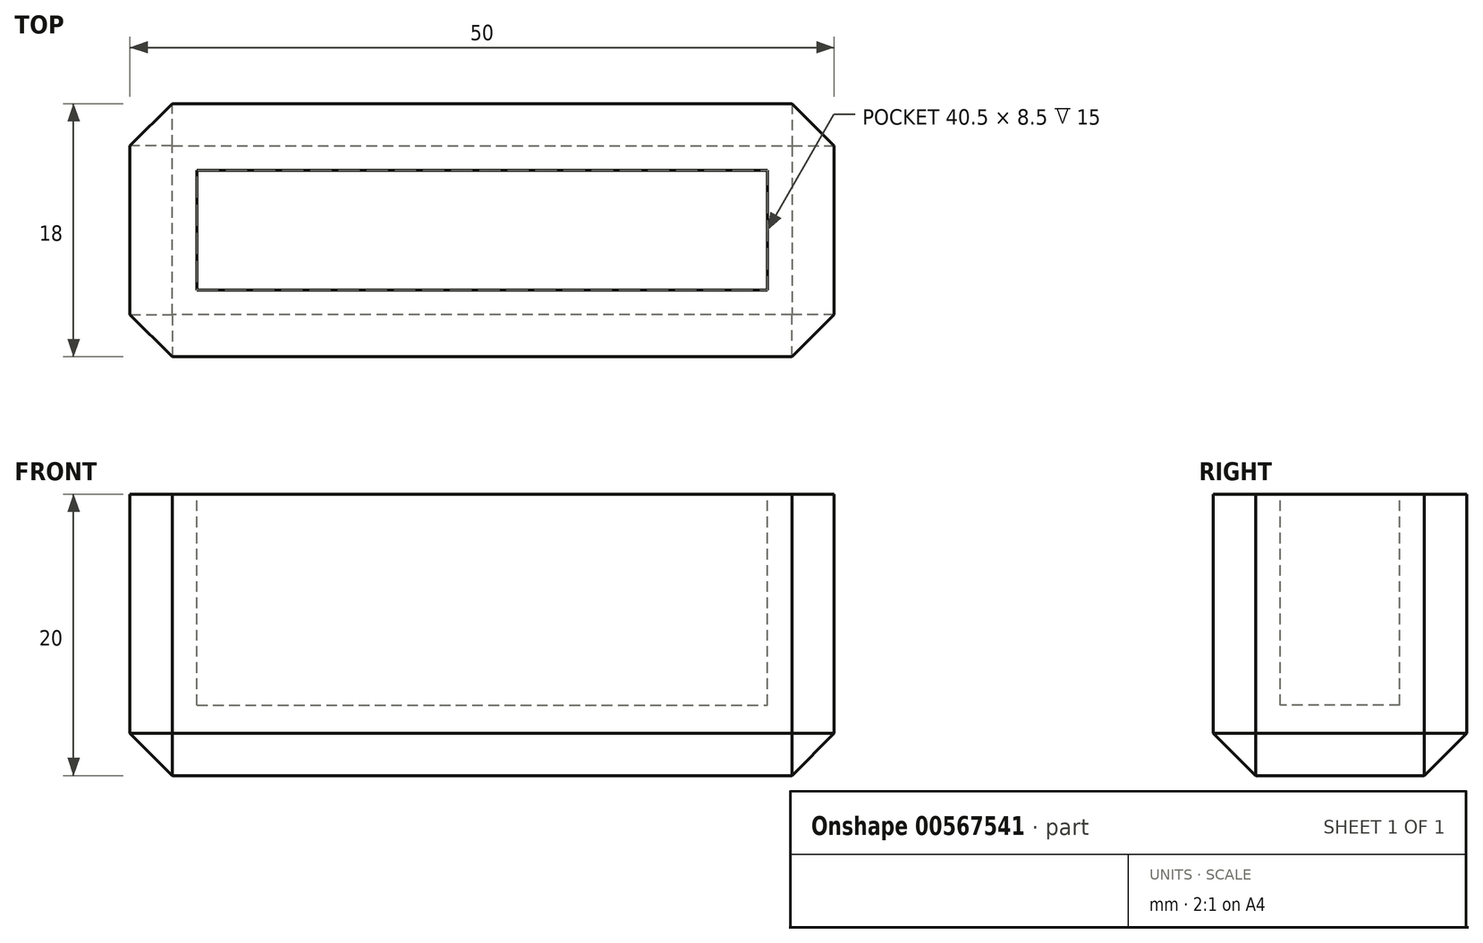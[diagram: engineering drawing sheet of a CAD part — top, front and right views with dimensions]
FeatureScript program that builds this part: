
annotation { "Feature Type Name" : "Feature", "Feature Type Description" : "" }
export const myFeature = defineFeature(function(context is Context, id is Id, definition is map)
    precondition{}
    {
        {
            var Q0;
            Q0=qCreatedBy(makeId("Top.planeOp"),FACE);
            var sketch = newSketch(context, id + "F0", { "sketchPlane" : qUnion([Q0])});
            skLineSegment(sketch, "E0.bottom", {"start": v(25, -9) * mm, "end": v(-25, -9) * mm});
            skLineSegment(sketch, "E0.top", {"start": v(25, 9) * mm, "end": v(-25, 9) * mm});
            skLineSegment(sketch, "E0.left", {"start": v(25, -9) * mm, "end": v(25, 9) * mm});
            skLineSegment(sketch, "E0.right", {"start": v(-25, -9) * mm, "end": v(-25, 9) * mm});
            skPoint(sketch, "E0.middle", {"position": v(0, 0) * mm});
            skSolve(sketch);
        }
        {
            var Q0;
            Q0 = qSketchRegion(id + "F0", true);
            extrude(context, id + "F1", {"entities" : qUnion([Q0]), "depth" : 20 * mm, "offsetDistance" : 25 * mm});
        }
        {
            var Q0;
            Q0=makeQuery(id+"F1.opExtrude","CAP_FACE",FACE,{"disambiguationData":[OSD([sQuery(id+"F0.wireOp",EDGE,"E0.bottom"),sQuery(id+"F0.wireOp",EDGE,"E0.top"),sQuery(id+"F0.wireOp",EDGE,"E0.left"),sQuery(id+"F0.wireOp",EDGE,"E0.right")])],"isStart":false});
            var sketch = newSketch(context, id + "F2", { "sketchPlane" : qUnion([Q0])});
            skLineSegment(sketch, "E1.bottom", {"start": v(20.25, -4.25) * mm, "end": v(-20.25, -4.25) * mm});
            skLineSegment(sketch, "E1.top", {"start": v(20.25, 4.25) * mm, "end": v(-20.25, 4.25) * mm});
            skLineSegment(sketch, "E1.left", {"start": v(20.25, -4.25) * mm, "end": v(20.25, 4.25) * mm});
            skLineSegment(sketch, "E1.right", {"start": v(-20.25, -4.25) * mm, "end": v(-20.25, 4.25) * mm});
            skPoint(sketch, "E1.middle", {"position": v(0, 0) * mm});
            skSolve(sketch);
        }
        {
            var Q0;
            Q0 = qSketchRegion(id + "F2", true);
            var Q1;
            Q1=makeQuery(id+"F1.opExtrude","CAP_FACE",FACE,{"disambiguationData":[OSD([sQuery(id+"F0.wireOp",EDGE,"E0.bottom"),sQuery(id+"F0.wireOp",EDGE,"E0.top"),sQuery(id+"F0.wireOp",EDGE,"E0.left"),sQuery(id+"F0.wireOp",EDGE,"E0.right")])],"isStart":true});
            extrude(context, id + "F3", {"entities" : qUnion([Q0]), "operationType" : NewBodyOperationType.REMOVE, "endBound" : BoundingType.UP_TO_SURFACE, "oppositeDirection" : true, "depth" : 25 * mm, "endBoundEntityFace" : qUnion([Q1]), "hasOffset" : true, "offsetDistance" : 5 * mm});
        }
        {
            var Q0;
            Q0=makeQuery(id+"F1.opExtrude","CAP_EDGE",EDGE,{"disambiguationData":[OSD([sQuery(id+"F0.wireOp",EDGE,"E0.bottom")])],"isStart":true});
            var Q1;
            Q1=makeQuery(id+"F1.opExtrude","CAP_EDGE",EDGE,{"disambiguationData":[OSD([sQuery(id+"F0.wireOp",EDGE,"E0.right")])],"isStart":true});
            var Q2;
            Q2=makeQuery(id+"F1.opExtrude","CAP_EDGE",EDGE,{"disambiguationData":[OSD([sQuery(id+"F0.wireOp",EDGE,"E0.top")])],"isStart":true});
            var Q3;
            Q3=makeQuery(id+"F1.opExtrude","CAP_EDGE",EDGE,{"disambiguationData":[OSD([sQuery(id+"F0.wireOp",EDGE,"E0.left")])],"isStart":true});
            var Q4;
            Q4=makeQuery(id+"F1.opExtrude","SWEPT_EDGE",EDGE,{"disambiguationData":[OSD([sQuery(id+"F0.wireOp",EDGE,"E0.bottom"),sQuery(id+"F0.wireOp",EDGE,"E0.right")])]});
            var Q5;
            Q5=makeQuery(id+"F1.opExtrude","SWEPT_EDGE",EDGE,{"disambiguationData":[OSD([sQuery(id+"F0.wireOp",EDGE,"E0.top"),sQuery(id+"F0.wireOp",EDGE,"E0.right")])]});
            var Q6;
            Q6=makeQuery(id+"F1.opExtrude","SWEPT_EDGE",EDGE,{"disambiguationData":[OSD([sQuery(id+"F0.wireOp",EDGE,"E0.top"),sQuery(id+"F0.wireOp",EDGE,"E0.left")])]});
            var Q7;
            Q7=makeQuery(id+"F1.opExtrude","SWEPT_EDGE",EDGE,{"disambiguationData":[OSD([sQuery(id+"F0.wireOp",EDGE,"E0.bottom"),sQuery(id+"F0.wireOp",EDGE,"E0.left")])]});
            chamfer(context, id + "F4", {"entities" : qUnion([Q0, Q1, Q2, Q3, Q4, Q5, Q6, Q7]), "width" : 3 * mm, "tangentPropagation" : true});
        }
    });
